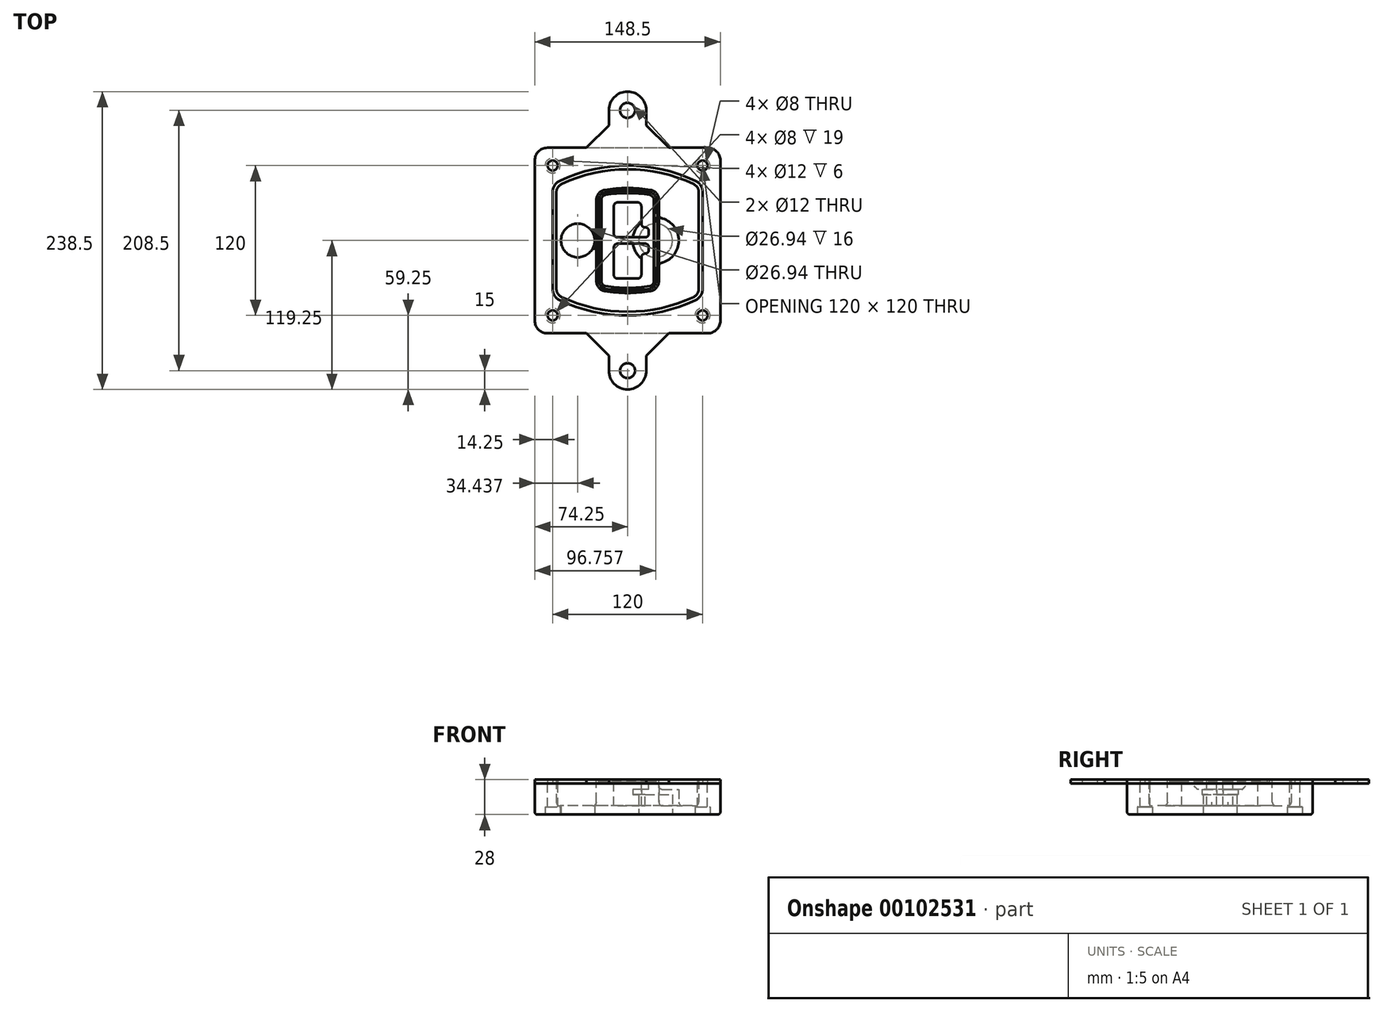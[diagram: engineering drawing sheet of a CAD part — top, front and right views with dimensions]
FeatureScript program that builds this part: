
annotation { "Feature Type Name" : "Feature", "Feature Type Description" : "" }
export const myFeature = defineFeature(function(context is Context, id is Id, definition is map)
    precondition{}
    {
        {
            var Q0;
            Q0=qCreatedBy(makeId("Top.planeOp"),FACE);
            var sketch = newSketch(context, id + "F0", { "sketchPlane" : qUnion([Q0])});
            skPoint(sketch, "E0.rect.middle", {"position": v(0, 0) * mm});
            skLineSegment(sketch, "E1.bottom", {"start": v(-64.25, -74.25) * mm, "end": v(64.25, -74.25) * mm});
            skLineSegment(sketch, "E1.top", {"start": v(-64.25, 74.25) * mm, "end": v(64.25, 74.25) * mm});
            skLineSegment(sketch, "E1.left", {"start": v(-74.25, -64.25) * mm, "end": v(-74.25, 64.25) * mm});
            skLineSegment(sketch, "E1.right", {"start": v(74.25, -64.25) * mm, "end": v(74.25, 64.25) * mm});
            skLineSegment(sketch, "E2", {"start": v(-74.25, 74.25) * mm, "end": v(74.25, -74.25) * mm, "construction": true});
            skLineSegment(sketch, "E3", {"start": v(74.25, 74.25) * mm, "end": v(-74.25, -74.25) * mm, "construction": true});
            skCircle(sketch, "E4", {"center": v(-60, 60) * mm, "radius": 4 * mm});
            skCircle(sketch, "E5", {"center": v(60, 60) * mm, "radius": 4 * mm});
            skCircle(sketch, "E6", {"center": v(60, -60) * mm, "radius": 4 * mm});
            skCircle(sketch, "E7", {"center": v(-60, -60) * mm, "radius": 4 * mm});
            skLineSegment(sketch, "E8", {"start": v(-60, 60) * mm, "end": v(60, 60) * mm, "construction": true});
            skLineSegment(sketch, "E9", {"start": v(60, 60) * mm, "end": v(60, -60) * mm, "construction": true});
            skLineSegment(sketch, "E10", {"start": v(60, -60) * mm, "end": v(-60, -60) * mm, "construction": true});
            skLineSegment(sketch, "E11", {"start": v(-60, -60) * mm, "end": v(-60, 60) * mm, "construction": true});
            skLineSegment(sketch, "E12", {"start": v(-60, 38.83) * mm, "end": v(-60, -38.83) * mm});
            skLineSegment(sketch, "E13", {"start": v(60, 38.83) * mm, "end": v(60, -38.83) * mm});
            skArc(sketch, "E14", {"start": v(54.26, 47.88) * mm, "mid": v(0, 60) * mm, "end": v(-54.26, 47.88) * mm});
            skArc(sketch, "E15", {"start": v(-54.26, -47.88) * mm, "mid": v(0, -60) * mm, "end": v(54.26, -47.88) * mm});
            skLineSegment(sketch, "E16", {"start": v(-60, 0) * mm, "end": v(60, 0) * mm, "construction": true});
            skPoint(sketch, "E17.visualSharp", {"position": v(-60, -45) * mm});
            skArc(sketch, "E17.filletArc", {"start": v(-60, -38.83) * mm, "mid": v(-58.44, -44.2) * mm, "end": v(-54.26, -47.88) * mm});
            skPoint(sketch, "E18.visualSharp", {"position": v(-60, 45) * mm});
            skArc(sketch, "E18.filletArc", {"start": v(-54.26, 47.88) * mm, "mid": v(-58.44, 44.2) * mm, "end": v(-60, 38.83) * mm});
            skPoint(sketch, "E19.visualSharp", {"position": v(60, 45) * mm});
            skArc(sketch, "E19.filletArc", {"start": v(60, 38.83) * mm, "mid": v(58.44, 44.2) * mm, "end": v(54.26, 47.88) * mm});
            skPoint(sketch, "E20.visualSharp", {"position": v(60, -45) * mm});
            skArc(sketch, "E20.filletArc", {"start": v(54.26, -47.88) * mm, "mid": v(58.44, -44.2) * mm, "end": v(60, -38.83) * mm});
            skPoint(sketch, "E21.visualSharp", {"position": v(-74.25, 74.25) * mm});
            skArc(sketch, "E21.filletArc", {"start": v(-64.25, 74.25) * mm, "mid": v(-71.32, 71.32) * mm, "end": v(-74.25, 64.25) * mm});
            skPoint(sketch, "E22.visualSharp", {"position": v(74.25, 74.25) * mm});
            skArc(sketch, "E22.filletArc", {"start": v(74.25, 64.25) * mm, "mid": v(71.32, 71.32) * mm, "end": v(64.25, 74.25) * mm});
            skPoint(sketch, "E23.visualSharp", {"position": v(74.25, -74.25) * mm});
            skArc(sketch, "E23.filletArc", {"start": v(64.25, -74.25) * mm, "mid": v(71.32, -71.32) * mm, "end": v(74.25, -64.25) * mm});
            skPoint(sketch, "E24.visualSharp", {"position": v(-74.25, -74.25) * mm});
            skArc(sketch, "E24.filletArc", {"start": v(-74.25, -64.25) * mm, "mid": v(-71.32, -71.32) * mm, "end": v(-64.25, -74.25) * mm});
            skArc(sketch, "E25.0", {"start": v(57, 38.83) * mm, "mid": v(55.9, 42.58) * mm, "end": v(52.98, 45.17) * mm});
            skLineSegment(sketch, "E25.1", {"start": v(57, 38.83) * mm, "end": v(57, -38.83) * mm});
            skArc(sketch, "E25.2", {"start": v(52.98, -45.17) * mm, "mid": v(55.9, -42.58) * mm, "end": v(57, -38.83) * mm});
            skArc(sketch, "E25.3", {"start": v(-52.98, -45.17) * mm, "mid": v(0, -57) * mm, "end": v(52.98, -45.17) * mm});
            skArc(sketch, "E25.4", {"start": v(-57, -38.83) * mm, "mid": v(-55.9, -42.58) * mm, "end": v(-52.98, -45.17) * mm});
            skArc(sketch, "E25.5", {"start": v(52.98, 45.17) * mm, "mid": v(0, 57) * mm, "end": v(-52.98, 45.17) * mm});
            skLineSegment(sketch, "E25.6", {"start": v(-57, 38.83) * mm, "end": v(-57, -38.83) * mm});
            skArc(sketch, "E25.7", {"start": v(-52.98, 45.17) * mm, "mid": v(-55.9, 42.58) * mm, "end": v(-57, 38.83) * mm});
            skArc(sketch, "E26.0", {"start": v(-55.96, 51.5) * mm, "mid": v(-61.82, 46.33) * mm, "end": v(-64, 38.83) * mm});
            skArc(sketch, "E26.1", {"start": v(55.96, 51.5) * mm, "mid": v(0, 64) * mm, "end": v(-55.96, 51.5) * mm});
            skArc(sketch, "E26.2", {"start": v(64, 38.83) * mm, "mid": v(61.82, 46.33) * mm, "end": v(55.96, 51.5) * mm});
            skLineSegment(sketch, "E26.3", {"start": v(64, 38.83) * mm, "end": v(64, -38.83) * mm});
            skArc(sketch, "E26.4", {"start": v(55.96, -51.5) * mm, "mid": v(61.82, -46.33) * mm, "end": v(64, -38.83) * mm});
            skLineSegment(sketch, "E26.5", {"start": v(-64, 38.83) * mm, "end": v(-64, -38.83) * mm});
            skArc(sketch, "E26.6", {"start": v(-55.96, -51.5) * mm, "mid": v(0, -64) * mm, "end": v(55.96, -51.5) * mm});
            skArc(sketch, "E26.7", {"start": v(-64, -38.83) * mm, "mid": v(-61.82, -46.33) * mm, "end": v(-55.96, -51.5) * mm});
            skSolve(sketch);
        }
        {
            var Q0;
            Q0=makeQuery(id+"F0.imprint","IMPRINT",FACE,{"disambiguationData":[TD([[makeQuery(id+"F0.imprint","IMPRINT",EDGE,{"derivedFrom":sQuery(id+"F0.wireOp",EDGE,"E1.bottom")}),1.0]])]});
            var Q1;
            Q1=makeQuery(id+"F0.imprint","IMPRINT",FACE,{"disambiguationData":[TD([[makeQuery(id+"F0.imprint","IMPRINT",EDGE,{"derivedFrom":sQuery(id+"F0.wireOp",EDGE,"E12")}),1.0]])]});
            var Q2;
            Q2=makeQuery(id+"F0.imprint","IMPRINT",FACE,{"disambiguationData":[TD([[makeQuery(id+"F0.imprint","IMPRINT",EDGE,{"derivedFrom":sQuery(id+"F0.wireOp",EDGE,"E25.0")}),1.0]])]});
            var Q3;
            Q3=makeQuery(id+"F0.imprint","IMPRINT",FACE,{"disambiguationData":[TD([[makeQuery(id+"F0.imprint","IMPRINT",EDGE,{"derivedFrom":sQuery(id+"F0.wireOp",EDGE,"E12")}),-1.0]])]});
            extrude(context, id + "F1", {"entities" : qUnion([Q0, Q1, Q2, Q3]), "oppositeDirection" : true, "depth" : 25 * mm});
        }
        {
            var Q0;
            Q0=makeQuery(id+"F0.imprint","IMPRINT",FACE,{"disambiguationData":[TD([[makeQuery(id+"F0.imprint","IMPRINT",EDGE,{"derivedFrom":sQuery(id+"F0.wireOp",EDGE,"E12")}),1.0]])]});
            extrude(context, id + "F2", {"entities" : qUnion([Q0]), "operationType" : NewBodyOperationType.ADD, "depth" : 3 * mm});
        }
        {
            var Q0;
            Q0=makeQuery(id+"F0.imprint","IMPRINT",FACE,{"disambiguationData":[TD([[makeQuery(id+"F0.imprint","IMPRINT",EDGE,{"derivedFrom":sQuery(id+"F0.wireOp",EDGE,"E25.0")}),1.0]])]});
            extrude(context, id + "F3", {"entities" : qUnion([Q0]), "operationType" : NewBodyOperationType.REMOVE, "oppositeDirection" : true, "depth" : 18 * mm});
        }
        {
            var Q0;
            Q0=makeQuery(id+"F2.opExtrude","CAP_FACE",FACE,{"disambiguationData":[OSD([sQuery(id+"F0.wireOp",EDGE,"E12"),sQuery(id+"F0.wireOp",EDGE,"E13"),sQuery(id+"F0.wireOp",EDGE,"E14"),sQuery(id+"F0.wireOp",EDGE,"E15"),sQuery(id+"F0.wireOp",EDGE,"E17.filletArc"),sQuery(id+"F0.wireOp",EDGE,"E18.filletArc"),sQuery(id+"F0.wireOp",EDGE,"E19.filletArc"),sQuery(id+"F0.wireOp",EDGE,"E20.filletArc"),sQuery(id+"F0.wireOp",EDGE,"E25.0"),sQuery(id+"F0.wireOp",EDGE,"E25.1"),sQuery(id+"F0.wireOp",EDGE,"E25.2"),sQuery(id+"F0.wireOp",EDGE,"E25.3"),sQuery(id+"F0.wireOp",EDGE,"E25.4"),sQuery(id+"F0.wireOp",EDGE,"E25.5"),sQuery(id+"F0.wireOp",EDGE,"E25.6"),sQuery(id+"F0.wireOp",EDGE,"E25.7")])],"isStart":false});
            var sketch = newSketch(context, id + "F4", { "sketchPlane" : qUnion([Q0])});
            skArc(sketch, "E27.0", {"start": v(-18.34, -40.45) * mm, "mid": v(0, -42) * mm, "end": v(18.34, -40.45) * mm});
            skArc(sketch, "E28.0", {"start": v(18.34, 40.45) * mm, "mid": v(0, 42) * mm, "end": v(-18.34, 40.45) * mm});
            skLineSegment(sketch, "E29", {"start": v(-25, 32.57) * mm, "end": v(-25, -32.57) * mm});
            skLineSegment(sketch, "E30", {"start": v(25, 32.57) * mm, "end": v(25, -32.57) * mm});
            skLineSegment(sketch, "E31", {"start": v(-25, 39.1) * mm, "end": v(25, 39.1) * mm, "construction": true});
            skLineSegment(sketch, "E32", {"start": v(-25, -39.1) * mm, "end": v(25, -39.1) * mm, "construction": true});
            skPoint(sketch, "E33.visualSharp", {"position": v(-25, 39.1) * mm});
            skArc(sketch, "E33.filletArc", {"start": v(-18.34, 40.45) * mm, "mid": v(-23.11, 37.73) * mm, "end": v(-25, 32.57) * mm});
            skPoint(sketch, "E34.visualSharp", {"position": v(25, 39.1) * mm});
            skArc(sketch, "E34.filletArc", {"start": v(25, 32.57) * mm, "mid": v(23.11, 37.73) * mm, "end": v(18.34, 40.45) * mm});
            skPoint(sketch, "E35.visualSharp", {"position": v(25, -39.1) * mm});
            skArc(sketch, "E35.filletArc", {"start": v(18.34, -40.45) * mm, "mid": v(23.11, -37.73) * mm, "end": v(25, -32.57) * mm});
            skPoint(sketch, "E36.visualSharp", {"position": v(-25, -39.1) * mm});
            skArc(sketch, "E36.filletArc", {"start": v(-25, -32.57) * mm, "mid": v(-23.11, -37.73) * mm, "end": v(-18.34, -40.45) * mm});
            skArc(sketch, "E37.0", {"start": v(52.98, 45.17) * mm, "mid": v(0, 57) * mm, "end": v(-52.98, 45.17) * mm});
            skArc(sketch, "E37.1", {"start": v(-52.98, 45.17) * mm, "mid": v(-55.9, 42.58) * mm, "end": v(-57, 38.83) * mm});
            skLineSegment(sketch, "E37.2", {"start": v(-57, 38.83) * mm, "end": v(-57, -38.83) * mm});
            skArc(sketch, "E37.3", {"start": v(-57, -38.83) * mm, "mid": v(-55.9, -42.58) * mm, "end": v(-52.98, -45.17) * mm});
            skArc(sketch, "E37.4", {"start": v(-52.98, -45.17) * mm, "mid": v(0, -57) * mm, "end": v(52.98, -45.17) * mm});
            skArc(sketch, "E37.5", {"start": v(52.98, -45.17) * mm, "mid": v(55.9, -42.58) * mm, "end": v(57, -38.83) * mm});
            skLineSegment(sketch, "E37.6", {"start": v(57, 38.83) * mm, "end": v(57, -38.83) * mm});
            skArc(sketch, "E37.7", {"start": v(57, 38.83) * mm, "mid": v(55.9, 42.58) * mm, "end": v(52.98, 45.17) * mm});
            skLineSegment(sketch, "E38.0", {"start": v(23, 32.57) * mm, "end": v(23, -32.57) * mm});
            skArc(sketch, "E38.1", {"start": v(18, -38.48) * mm, "mid": v(21.58, -36.44) * mm, "end": v(23, -32.57) * mm});
            skArc(sketch, "E38.2", {"start": v(-18, -38.48) * mm, "mid": v(0, -40) * mm, "end": v(18, -38.48) * mm});
            skArc(sketch, "E38.3", {"start": v(-23, -32.57) * mm, "mid": v(-21.58, -36.44) * mm, "end": v(-18, -38.48) * mm});
            skLineSegment(sketch, "E38.4", {"start": v(-23, 32.57) * mm, "end": v(-23, -32.57) * mm});
            skArc(sketch, "E38.5", {"start": v(23, 32.57) * mm, "mid": v(21.58, 36.44) * mm, "end": v(18, 38.48) * mm});
            skArc(sketch, "E38.6", {"start": v(-18, 38.48) * mm, "mid": v(-21.58, 36.44) * mm, "end": v(-23, 32.57) * mm});
            skArc(sketch, "E38.7", {"start": v(18, 38.48) * mm, "mid": v(0, 40) * mm, "end": v(-18, 38.48) * mm});
            skArc(sketch, "E39.0", {"start": v(21, 32.57) * mm, "mid": v(20.06, 35.15) * mm, "end": v(17.67, 36.5) * mm});
            skLineSegment(sketch, "E39.1", {"start": v(21, 32.57) * mm, "end": v(21, -32.57) * mm});
            skArc(sketch, "E39.2", {"start": v(17.67, -36.5) * mm, "mid": v(20.06, -35.15) * mm, "end": v(21, -32.57) * mm});
            skArc(sketch, "E39.3", {"start": v(-17.67, -36.5) * mm, "mid": v(0, -38) * mm, "end": v(17.67, -36.5) * mm});
            skArc(sketch, "E39.4", {"start": v(-21, -32.57) * mm, "mid": v(-20.06, -35.15) * mm, "end": v(-17.67, -36.5) * mm});
            skArc(sketch, "E39.5", {"start": v(17.67, 36.5) * mm, "mid": v(0, 38) * mm, "end": v(-17.67, 36.5) * mm});
            skLineSegment(sketch, "E39.6", {"start": v(-21, 32.57) * mm, "end": v(-21, -32.57) * mm});
            skArc(sketch, "E39.7", {"start": v(-17.67, 36.5) * mm, "mid": v(-20.06, 35.15) * mm, "end": v(-21, 32.57) * mm});
            skLineSegment(sketch, "E40", {"start": v(-25, 0) * mm, "end": v(25, 0) * mm, "construction": true});
            skLineSegment(sketch, "E41", {"start": v(-11, 5.5) * mm, "end": v(-11, 27.5) * mm});
            skLineSegment(sketch, "E42", {"start": v(-8, 30.5) * mm, "end": v(8, 30.5) * mm});
            skLineSegment(sketch, "E43", {"start": v(11, 27.5) * mm, "end": v(11, 13.5) * mm});
            skLineSegment(sketch, "E44", {"start": v(14, 10.5) * mm, "end": v(14, 10.5) * mm});
            skLineSegment(sketch, "E45", {"start": v(17, 7.5) * mm, "end": v(17, 5.5) * mm});
            skLineSegment(sketch, "E46", {"start": v(14, 2.5) * mm, "end": v(-8, 2.5) * mm});
            skPoint(sketch, "E47.visualSharp", {"position": v(-11, 30.5) * mm});
            skArc(sketch, "E47.filletArc", {"start": v(-8, 30.5) * mm, "mid": v(-10.12, 29.62) * mm, "end": v(-11, 27.5) * mm});
            skPoint(sketch, "E48.visualSharp", {"position": v(11, 30.5) * mm});
            skArc(sketch, "E48.filletArc", {"start": v(11, 27.5) * mm, "mid": v(10.12, 29.62) * mm, "end": v(8, 30.5) * mm});
            skPoint(sketch, "E49.visualSharp", {"position": v(11, 10.5) * mm});
            skArc(sketch, "E49.filletArc", {"start": v(11, 13.5) * mm, "mid": v(11.88, 11.38) * mm, "end": v(14, 10.5) * mm});
            skPoint(sketch, "E50.visualSharp", {"position": v(17, 10.5) * mm});
            skArc(sketch, "E50.filletArc", {"start": v(17, 7.5) * mm, "mid": v(16.12, 9.62) * mm, "end": v(14, 10.5) * mm});
            skPoint(sketch, "E51.visualSharp", {"position": v(17, 2.5) * mm});
            skArc(sketch, "E51.filletArc", {"start": v(14, 2.5) * mm, "mid": v(16.12, 3.38) * mm, "end": v(17, 5.5) * mm});
            skPoint(sketch, "E52.visualSharp", {"position": v(-11, 2.5) * mm});
            skArc(sketch, "E52.filletArc", {"start": v(-11, 5.5) * mm, "mid": v(-10.12, 3.38) * mm, "end": v(-8, 2.5) * mm});
            skLineSegment(sketch, "E53.0.MirrorCS", {"start": v(14, -2.5) * mm, "end": v(-8, -2.5) * mm});
            skArc(sketch, "E54.0.MirrorCS", {"start": v(-11, -5.5) * mm, "mid": v(-10.12, -3.38) * mm, "end": v(-8, -2.5) * mm});
            skLineSegment(sketch, "E55.0.MirrorCS", {"start": v(-11, -5.5) * mm, "end": v(-11, -27.5) * mm});
            skArc(sketch, "E56.0.MirrorCS", {"start": v(-8, -30.5) * mm, "mid": v(-10.12, -29.62) * mm, "end": v(-11, -27.5) * mm});
            skLineSegment(sketch, "E57.0.MirrorCS", {"start": v(-8, -30.5) * mm, "end": v(8, -30.5) * mm});
            skArc(sketch, "E58.0.MirrorCS", {"start": v(11, -27.5) * mm, "mid": v(10.12, -29.62) * mm, "end": v(8, -30.5) * mm});
            skLineSegment(sketch, "E59.0.MirrorCS", {"start": v(11, -27.5) * mm, "end": v(11, -13.5) * mm});
            skArc(sketch, "E60.0.MirrorCS", {"start": v(11, -13.5) * mm, "mid": v(11.88, -11.38) * mm, "end": v(14, -10.5) * mm});
            skArc(sketch, "E61.0.MirrorCS", {"start": v(17, -7.5) * mm, "mid": v(16.12, -9.62) * mm, "end": v(14, -10.5) * mm});
            skLineSegment(sketch, "E62.0.MirrorCS", {"start": v(17, -7.5) * mm, "end": v(17, -5.5) * mm});
            skArc(sketch, "E63.0.MirrorCS", {"start": v(14, -2.5) * mm, "mid": v(16.12, -3.38) * mm, "end": v(17, -5.5) * mm});
            skSolve(sketch);
        }
        {
            var Q0;
            Q0=makeQuery(id+"F4.imprint","IMPRINT",FACE,{"disambiguationData":[TD([[makeQuery(id+"F4.imprint","IMPRINT",EDGE,{"derivedFrom":sQuery(id+"F4.wireOp",EDGE,"E27.0")}),1.0]])]});
            var Q1;
            Q1=makeQuery(id+"F4.imprint","IMPRINT",FACE,{"disambiguationData":[TD([[makeQuery(id+"F4.imprint","IMPRINT",EDGE,{"derivedFrom":sQuery(id+"F4.wireOp",EDGE,"E38.0")}),-1.0]])]});
            var Q2;
            Q2=makeQuery(id+"F4.imprint","IMPRINT",FACE,{"disambiguationData":[TD([[makeQuery(id+"F4.imprint","IMPRINT",EDGE,{"derivedFrom":sQuery(id+"F4.wireOp",EDGE,"E39.0")}),1.0]])]});
            extrude(context, id + "F5", {"entities" : qUnion([Q0, Q1, Q2]), "operationType" : NewBodyOperationType.ADD, "endBound" : BoundingType.UP_TO_NEXT, "oppositeDirection" : true, "depth" : 25 * mm});
        }
        {
            var Q0;
            Q0=makeQuery(id+"F4.imprint","IMPRINT",FACE,{"disambiguationData":[TD([[makeQuery(id+"F4.imprint","IMPRINT",EDGE,{"derivedFrom":sQuery(id+"F4.wireOp",EDGE,"E38.0")}),-1.0]])]});
            extrude(context, id + "F6", {"entities" : qUnion([Q0]), "operationType" : NewBodyOperationType.REMOVE, "oppositeDirection" : true, "depth" : 2 * mm});
        }
        {
            var Q0;
            Q0=makeQuery(id+"F1.opExtrude","CAP_FACE",FACE,{"disambiguationData":[OSD([sQuery(id+"F0.wireOp",EDGE,"E1.bottom"),sQuery(id+"F0.wireOp",EDGE,"E1.top"),sQuery(id+"F0.wireOp",EDGE,"E1.left"),sQuery(id+"F0.wireOp",EDGE,"E1.right"),sQuery(id+"F0.wireOp",EDGE,"E4"),sQuery(id+"F0.wireOp",EDGE,"E5"),sQuery(id+"F0.wireOp",EDGE,"E6"),sQuery(id+"F0.wireOp",EDGE,"E7"),sQuery(id+"F0.wireOp",EDGE,"E21.filletArc"),sQuery(id+"F0.wireOp",EDGE,"E22.filletArc"),sQuery(id+"F0.wireOp",EDGE,"E23.filletArc"),sQuery(id+"F0.wireOp",EDGE,"E24.filletArc")])],"isStart":false});
            var sketch = newSketch(context, id + "F7", { "sketchPlane" : qUnion([Q0])});
            skCircle(sketch, "E64", {"center": v(22.5, 0) * mm, "radius": 13.47 * mm});
            skCircle(sketch, "E65", {"center": v(-39.81, 0) * mm, "radius": 13.47 * mm});
            skLineSegment(sketch, "E66", {"start": v(74.25, 0) * mm, "end": v(-74.25, 0) * mm});
            skCircle(sketch, "E67", {"center": v(22.5, 0) * mm, "radius": 18.47 * mm});
            skCircle(sketch, "E68", {"center": v(60, -60) * mm, "radius": 6 * mm});
            skCircle(sketch, "E69", {"center": v(-60, -60) * mm, "radius": 6 * mm});
            skCircle(sketch, "E70", {"center": v(-60, 60) * mm, "radius": 6 * mm});
            skCircle(sketch, "E71", {"center": v(60, 60) * mm, "radius": 6 * mm});
            skSolve(sketch);
        }
        {
            var Q0;
            {var subQ1=sQuery(id+"F7.wireOp",EDGE,"E66");var subQ4=sQuery(id+"F7.wireOp",EDGE,"E64");var subQ6=makeQuery(id+"F7.imprint","INTERSECT",VERTEX,{"disambiguationData":[OD(0.0)],"derivedFrom":[subQ4,subQ1]});Q0=makeQuery(id+"F7.imprint","IMPRINT",FACE,{"disambiguationData":[TD([[makeQuery(id+"F7.imprint","IMPRINT",EDGE,{"disambiguationData":[TD([[subQ6,-1.0]])],"derivedFrom":subQ4}),-1.0]])]});}
            var Q1;
            {var subQ0=sQuery(id+"F7.wireOp",EDGE,"E66");var subQ1=sQuery(id+"F7.wireOp",EDGE,"E64");var subQ3=makeQuery(id+"F7.imprint","INTERSECT",VERTEX,{"disambiguationData":[OD(0.0)],"derivedFrom":[subQ1,subQ0]});Q1=makeQuery(id+"F7.imprint","IMPRINT",FACE,{"disambiguationData":[TD([[makeQuery(id+"F7.imprint","IMPRINT",EDGE,{"disambiguationData":[TD([[subQ3,-1.0]])],"derivedFrom":subQ1}),1.0]])]});}
            var Q2;
            {var subQ0=sQuery(id+"F7.wireOp",EDGE,"E66");var subQ1=sQuery(id+"F7.wireOp",EDGE,"E64");var subQ3=makeQuery(id+"F7.imprint","INTERSECT",VERTEX,{"disambiguationData":[OD(0.0)],"derivedFrom":[subQ1,subQ0]});Q2=makeQuery(id+"F7.imprint","IMPRINT",FACE,{"disambiguationData":[TD([[makeQuery(id+"F7.imprint","IMPRINT",EDGE,{"disambiguationData":[TD([[subQ3,1.0]])],"derivedFrom":subQ1}),1.0]])]});}
            var Q3;
            {var subQ1=sQuery(id+"F7.wireOp",EDGE,"E66");var subQ4=sQuery(id+"F7.wireOp",EDGE,"E64");var subQ6=makeQuery(id+"F7.imprint","INTERSECT",VERTEX,{"disambiguationData":[OD(0.0)],"derivedFrom":[subQ4,subQ1]});Q3=makeQuery(id+"F7.imprint","IMPRINT",FACE,{"disambiguationData":[TD([[makeQuery(id+"F7.imprint","IMPRINT",EDGE,{"disambiguationData":[TD([[subQ6,1.0]])],"derivedFrom":subQ4}),-1.0]])]});}
            extrude(context, id + "F8", {"entities" : qUnion([Q0, Q1, Q2, Q3]), "operationType" : NewBodyOperationType.ADD, "oppositeDirection" : true, "depth" : 20 * mm});
        }
        {
            var Q0;
            {var subQ0=sQuery(id+"F7.wireOp",EDGE,"E66");var subQ1=sQuery(id+"F7.wireOp",EDGE,"E64");var subQ3=makeQuery(id+"F7.imprint","INTERSECT",VERTEX,{"disambiguationData":[OD(0.0)],"derivedFrom":[subQ1,subQ0]});Q0=makeQuery(id+"F7.imprint","IMPRINT",FACE,{"disambiguationData":[TD([[makeQuery(id+"F7.imprint","IMPRINT",EDGE,{"disambiguationData":[TD([[subQ3,-1.0]])],"derivedFrom":subQ1}),1.0]])]});}
            var Q1;
            {var subQ0=sQuery(id+"F7.wireOp",EDGE,"E66");var subQ1=sQuery(id+"F7.wireOp",EDGE,"E64");var subQ3=makeQuery(id+"F7.imprint","INTERSECT",VERTEX,{"disambiguationData":[OD(0.0)],"derivedFrom":[subQ1,subQ0]});Q1=makeQuery(id+"F7.imprint","IMPRINT",FACE,{"disambiguationData":[TD([[makeQuery(id+"F7.imprint","IMPRINT",EDGE,{"disambiguationData":[TD([[subQ3,1.0]])],"derivedFrom":subQ1}),1.0]])]});}
            extrude(context, id + "F9", {"entities" : qUnion([Q0, Q1]), "operationType" : NewBodyOperationType.REMOVE, "oppositeDirection" : true, "depth" : 16 * mm});
        }
        {
            var Q0;
            {var subQ0=sQuery(id+"F7.wireOp",EDGE,"E66");var subQ1=sQuery(id+"F7.wireOp",EDGE,"E65");var subQ3=makeQuery(id+"F7.imprint","INTERSECT",VERTEX,{"disambiguationData":[OD(0.0)],"derivedFrom":[subQ1,subQ0]});Q0=makeQuery(id+"F7.imprint","IMPRINT",FACE,{"disambiguationData":[TD([[makeQuery(id+"F7.imprint","IMPRINT",EDGE,{"disambiguationData":[TD([[subQ3,-1.0]])],"derivedFrom":subQ1}),1.0]])]});}
            var Q1;
            {var subQ0=sQuery(id+"F7.wireOp",EDGE,"E66");var subQ1=sQuery(id+"F7.wireOp",EDGE,"E65");var subQ3=makeQuery(id+"F7.imprint","INTERSECT",VERTEX,{"disambiguationData":[OD(0.0)],"derivedFrom":[subQ1,subQ0]});Q1=makeQuery(id+"F7.imprint","IMPRINT",FACE,{"disambiguationData":[TD([[makeQuery(id+"F7.imprint","IMPRINT",EDGE,{"disambiguationData":[TD([[subQ3,1.0]])],"derivedFrom":subQ1}),1.0]])]});}
            extrude(context, id + "F10", {"entities" : qUnion([Q0, Q1]), "operationType" : NewBodyOperationType.REMOVE, "oppositeDirection" : true, "depth" : 25 * mm});
        }
        {
            var Q0;
            Q0=makeQuery(id+"F7.imprint","IMPRINT",FACE,{"disambiguationData":[TD([[makeQuery(id+"F7.imprint","IMPRINT",EDGE,{"derivedFrom":sQuery(id+"F7.wireOp",EDGE,"E68")}),1.0]])]});
            var Q1;
            Q1=makeQuery(id+"F7.imprint","IMPRINT",FACE,{"disambiguationData":[TD([[makeQuery(id+"F7.imprint","IMPRINT",EDGE,{"derivedFrom":makeQuery(id+"F1.opExtrude","CAP_EDGE",EDGE,{"disambiguationData":[OSD([sQuery(id+"F0.wireOp",EDGE,"E5")])],"isStart":false})}),-1.0]])]});
            var Q2;
            Q2=makeQuery(id+"F7.imprint","IMPRINT",FACE,{"disambiguationData":[TD([[makeQuery(id+"F7.imprint","IMPRINT",EDGE,{"derivedFrom":sQuery(id+"F7.wireOp",EDGE,"E69")}),1.0]])]});
            var Q3;
            Q3=makeQuery(id+"F7.imprint","IMPRINT",FACE,{"disambiguationData":[TD([[makeQuery(id+"F7.imprint","IMPRINT",EDGE,{"derivedFrom":makeQuery(id+"F1.opExtrude","CAP_EDGE",EDGE,{"disambiguationData":[OSD([sQuery(id+"F0.wireOp",EDGE,"E4")])],"isStart":false})}),-1.0]])]});
            var Q4;
            Q4=makeQuery(id+"F7.imprint","IMPRINT",FACE,{"disambiguationData":[TD([[makeQuery(id+"F7.imprint","IMPRINT",EDGE,{"derivedFrom":sQuery(id+"F7.wireOp",EDGE,"E70")}),1.0]])]});
            var Q5;
            Q5=makeQuery(id+"F7.imprint","IMPRINT",FACE,{"disambiguationData":[TD([[makeQuery(id+"F7.imprint","IMPRINT",EDGE,{"derivedFrom":makeQuery(id+"F1.opExtrude","CAP_EDGE",EDGE,{"disambiguationData":[OSD([sQuery(id+"F0.wireOp",EDGE,"E7")])],"isStart":false})}),-1.0]])]});
            var Q6;
            Q6=makeQuery(id+"F7.imprint","IMPRINT",FACE,{"disambiguationData":[TD([[makeQuery(id+"F7.imprint","IMPRINT",EDGE,{"derivedFrom":sQuery(id+"F7.wireOp",EDGE,"E71")}),1.0]])]});
            var Q7;
            Q7=makeQuery(id+"F7.imprint","IMPRINT",FACE,{"disambiguationData":[TD([[makeQuery(id+"F7.imprint","IMPRINT",EDGE,{"derivedFrom":makeQuery(id+"F1.opExtrude","CAP_EDGE",EDGE,{"disambiguationData":[OSD([sQuery(id+"F0.wireOp",EDGE,"E6")])],"isStart":false})}),-1.0]])]});
            extrude(context, id + "F11", {"entities" : qUnion([Q0, Q1, Q2, Q3, Q4, Q5, Q6, Q7]), "operationType" : NewBodyOperationType.REMOVE, "oppositeDirection" : true, "depth" : 6 * mm});
        }
        {
            var Q0;
            Q0=makeQuery(id+"F9.boolean.opBoolean","COPY",FACE,{"derivedFrom":makeQuery(id+"F9.opExtrude","CAP_FACE",FACE,{"disambiguationData":[OSD([sQuery(id+"F7.wireOp",EDGE,"E64")])],"isStart":false})});
            var sketch = newSketch(context, id + "F12", { "sketchPlane" : qUnion([Q0])});
            skArc(sketch, "E72.0", {"start": v(11, 14.45) * mm, "mid": v(6.45, 9.13) * mm, "end": v(4.2, 2.5) * mm});
            skArc(sketch, "E72.1", {"start": v(4.2, -2.5) * mm, "mid": v(6.45, -9.13) * mm, "end": v(11, -14.45) * mm});
            skLineSegment(sketch, "E73", {"start": v(4.2, -2.5) * mm, "end": v(14, -2.5) * mm});
            skLineSegment(sketch, "E74.0", {"start": v(14, 2.5) * mm, "end": v(4.2, 2.5) * mm});
            skArc(sketch, "E74.1", {"start": v(14, 2.5) * mm, "mid": v(16.12, 3.38) * mm, "end": v(17, 5.5) * mm});
            skLineSegment(sketch, "E74.2", {"start": v(17, 7.5) * mm, "end": v(17, 5.5) * mm});
            skArc(sketch, "E74.3", {"start": v(17, 7.5) * mm, "mid": v(16.12, 9.62) * mm, "end": v(14, 10.5) * mm});
            skArc(sketch, "E74.4", {"start": v(11, 13.5) * mm, "mid": v(11.88, 11.38) * mm, "end": v(14, 10.5) * mm});
            skLineSegment(sketch, "E74.5", {"start": v(11, 14.45) * mm, "end": v(11, 13.5) * mm});
            skLineSegment(sketch, "E74.7", {"start": v(14, -2.5) * mm, "end": v(4.2, -2.5) * mm});
            skArc(sketch, "E74.8", {"start": v(14, -2.5) * mm, "mid": v(16.12, -3.38) * mm, "end": v(17, -5.5) * mm});
            skLineSegment(sketch, "E74.9", {"start": v(17, -7.5) * mm, "end": v(17, -5.5) * mm});
            skArc(sketch, "E74.10", {"start": v(17, -7.5) * mm, "mid": v(16.12, -9.62) * mm, "end": v(14, -10.5) * mm});
            skArc(sketch, "E74.11", {"start": v(11, -13.5) * mm, "mid": v(11.88, -11.38) * mm, "end": v(14, -10.5) * mm});
            skLineSegment(sketch, "E74.12", {"start": v(11, -14.45) * mm, "end": v(11, -13.5) * mm});
            skPoint(sketch, "E75.orphan", {"position": v(11, -27.5) * mm});
            skPoint(sketch, "E76.orphan", {"position": v(-8, -2.5) * mm});
            skPoint(sketch, "E77.orphan", {"position": v(-8, 2.5) * mm});
            skPoint(sketch, "E78.orphan", {"position": v(11, 27.5) * mm});
            skSolve(sketch);
        }
        {
            var Q0;
            {var subQ7=sQuery(id+"F12.wireOp",EDGE,"E72.0");var subQ14=sQuery(id+"F12.wireOp",EDGE,"E72.1");var subQ16=sQuery(id+"F12.wireOp",EDGE,"E74.1");var subQ18=sQuery(id+"F12.wireOp",EDGE,"E74.8");Q0=qUnion([makeQuery(id+"F12.imprint","IMPRINT",FACE,{"disambiguationData":[TD([[makeQuery(id+"F12.imprint","IMPRINT",EDGE,{"derivedFrom":subQ7}),1.0]])]}),makeQuery(id+"F12.imprint","IMPRINT",FACE,{"disambiguationData":[TD([[makeQuery(id+"F12.imprint","IMPRINT",EDGE,{"derivedFrom":subQ14}),1.0]])]}),makeQuery(id+"F12.imprint","IMPRINT",FACE,{"disambiguationData":[TD([[makeQuery(id+"F12.imprint","IMPRINT",EDGE,{"derivedFrom":subQ16}),1.0]])]}),makeQuery(id+"F12.imprint","IMPRINT",FACE,{"disambiguationData":[TD([[makeQuery(id+"F12.imprint","IMPRINT",EDGE,{"derivedFrom":subQ18}),-1.0]])]})]);}
            var Q1;
            Q1=makeQuery(id+"F5.boolean.opBoolean","SPLIT",FACE,{"disambiguationData":[TD([makeQuery(id+"F5.opExtrude","SWEPT_FACE",FACE,{"disambiguationData":[OSD([sQuery(id+"F4.wireOp",EDGE,"E41")])]})])],"derivedFrom":makeQuery(id+"F3.boolean.opBoolean","COPY",FACE,{"derivedFrom":makeQuery(id+"F3.opExtrude","CAP_FACE",FACE,{"disambiguationData":[OSD([sQuery(id+"F0.wireOp",EDGE,"E25.0"),sQuery(id+"F0.wireOp",EDGE,"E25.1"),sQuery(id+"F0.wireOp",EDGE,"E25.2"),sQuery(id+"F0.wireOp",EDGE,"E25.3"),sQuery(id+"F0.wireOp",EDGE,"E25.4"),sQuery(id+"F0.wireOp",EDGE,"E25.5"),sQuery(id+"F0.wireOp",EDGE,"E25.6"),sQuery(id+"F0.wireOp",EDGE,"E25.7")])],"isStart":false})})});
            extrude(context, id + "F13", {"entities" : qUnion([Q0]), "operationType" : NewBodyOperationType.REMOVE, "endBound" : BoundingType.UP_TO_SURFACE, "endBoundEntityFace" : qUnion([Q1]), "depth" : 25 * mm});
        }
        {
            var Q0;
            Q0=makeQuery(id+"F3.boolean.opBoolean","COPY",EDGE,{"derivedFrom":makeQuery(id+"F3.opExtrude","CAP_EDGE",EDGE,{"disambiguationData":[OSD([sQuery(id+"F0.wireOp",EDGE,"E25.6")])],"isStart":false})});
            var Q1;
            Q1=makeQuery(id+"F8.boolean.opBoolean","INTERSECT",EDGE,{"derivedFrom":[makeQuery(id+"F5.opExtrude","SWEPT_FACE",FACE,{"disambiguationData":[OSD([sQuery(id+"F4.wireOp",EDGE,"E30")])]}),makeQuery(id+"F8.opExtrude","CAP_FACE",FACE,{"disambiguationData":[OSD([sQuery(id+"F7.wireOp",EDGE,"E67")])],"isStart":false})]});
            var Q2;
            Q2=makeQuery(id+"F8.boolean.opBoolean","INTERSECT",EDGE,{"disambiguationData":[OD(1.0)],"derivedFrom":[makeQuery(id+"F5.opExtrude","SWEPT_FACE",FACE,{"disambiguationData":[OSD([sQuery(id+"F4.wireOp",EDGE,"E30")])]}),makeQuery(id+"F8.opExtrude","SWEPT_FACE",FACE,{"disambiguationData":[OSD([sQuery(id+"F7.wireOp",EDGE,"E67")])]})]});
            var Q3;
            {var subQ0=sQuery(id+"F4.wireOp",EDGE,"E30");Q3=makeQuery(id+"F8.boolean.opBoolean","SPLIT",EDGE,{"disambiguationData":[TD([makeQuery(id+"F5.opExtrude","SWEPT_FACE",FACE,{"disambiguationData":[OSD([sQuery(id+"F4.wireOp",EDGE,"E35.filletArc")])]})])],"derivedFrom":makeQuery(id+"F5.opExtrude","CAP_EDGE",EDGE,{"disambiguationData":[OSD([subQ0])],"isStart":false})});}
            var Q4;
            {var subQ0=sQuery(id+"F0.wireOp",EDGE,"E25.7");var subQ1=sQuery(id+"F0.wireOp",EDGE,"E25.1");var subQ2=sQuery(id+"F0.wireOp",EDGE,"E25.6");var subQ3=sQuery(id+"F0.wireOp",EDGE,"E25.5");var subQ4=sQuery(id+"F0.wireOp",EDGE,"E25.4");var subQ5=sQuery(id+"F0.wireOp",EDGE,"E25.0");var subQ6=sQuery(id+"F0.wireOp",EDGE,"E25.2");var subQ7=sQuery(id+"F0.wireOp",EDGE,"E25.3");Q4=makeQuery(id+"F8.boolean.opBoolean","INTERSECT",EDGE,{"derivedFrom":[makeQuery(id+"F5.boolean.opBoolean","SPLIT",FACE,{"disambiguationData":[TD([makeQuery(id+"F2.opExtrude","SWEPT_FACE",FACE,{"disambiguationData":[OSD([subQ5])]})])],"derivedFrom":makeQuery(id+"F3.boolean.opBoolean","COPY",FACE,{"derivedFrom":makeQuery(id+"F3.opExtrude","CAP_FACE",FACE,{"disambiguationData":[OSD([subQ5,subQ1,subQ6,subQ7,subQ4,subQ3,subQ2,subQ0])],"isStart":false})})}),makeQuery(id+"F8.opExtrude","SWEPT_FACE",FACE,{"disambiguationData":[OSD([sQuery(id+"F7.wireOp",EDGE,"E67")])]})]});}
            var Q5;
            Q5=makeQuery(id+"F8.boolean.opBoolean","INTERSECT",EDGE,{"disambiguationData":[OD(0.0)],"derivedFrom":[makeQuery(id+"F5.opExtrude","SWEPT_FACE",FACE,{"disambiguationData":[OSD([sQuery(id+"F4.wireOp",EDGE,"E30")])]}),makeQuery(id+"F8.opExtrude","SWEPT_FACE",FACE,{"disambiguationData":[OSD([sQuery(id+"F7.wireOp",EDGE,"E67")])]})]});
            fillet(context, id + "F14", {"entities" : qUnion([Q0, Q1, Q2, Q3, Q4, Q5]), "radius" : 3 * mm, "tangentPropagation" : true, "allowEdgeOverflow" : false});
        }
        {
            var Q0;
            Q0=makeQuery(id+"F1.opExtrude","CAP_EDGE",EDGE,{"disambiguationData":[OSD([sQuery(id+"F0.wireOp",EDGE,"E1.bottom")])],"isStart":false});
            fillet(context, id + "F15", {"entities" : qUnion([Q0]), "radius" : 2 * mm, "tangentPropagation" : true, "allowEdgeOverflow" : false});
        }
        {
            var Q0;
            {var subQ0=sQuery(id+"F0.wireOp",EDGE,"E22.filletArc");var subQ1=sQuery(id+"F0.wireOp",EDGE,"E7");var subQ2=sQuery(id+"F0.wireOp",EDGE,"E6");var subQ3=sQuery(id+"F0.wireOp",EDGE,"E5");var subQ4=sQuery(id+"F0.wireOp",EDGE,"E4");var subQ5=sQuery(id+"F0.wireOp",EDGE,"E1.bottom");var subQ6=sQuery(id+"F0.wireOp",EDGE,"E21.filletArc");var subQ7=sQuery(id+"F0.wireOp",EDGE,"E1.top");var subQ8=sQuery(id+"F0.wireOp",EDGE,"E1.left");var subQ9=sQuery(id+"F0.wireOp",EDGE,"E1.right");var subQ10=sQuery(id+"F0.wireOp",EDGE,"E23.filletArc");var subQ11=sQuery(id+"F0.wireOp",EDGE,"E24.filletArc");Q0=makeQuery(id+"F2.boolean.opBoolean","SPLIT",FACE,{"disambiguationData":[TD([makeQuery(id+"F1.opExtrude","SWEPT_FACE",FACE,{"disambiguationData":[OSD([subQ5])]})])],"derivedFrom":makeQuery(id+"F1.opExtrude","CAP_FACE",FACE,{"disambiguationData":[OSD([subQ5,subQ7,subQ8,subQ9,subQ4,subQ3,subQ2,subQ1,subQ6,subQ0,subQ10,subQ11])],"isStart":true})});}
            var sketch = newSketch(context, id + "F16", { "sketchPlane" : qUnion([Q0])});
            skLineSegment(sketch, "E79", {"start": v(0, 74.25) * mm, "end": v(0, 104.25) * mm, "construction": true});
            skPoint(sketch, "E79.endSnap0", {"position": v(0, 74.25) * mm});
            skCircle(sketch, "E80", {"center": v(0, 104.25) * mm, "radius": 6 * mm});
            skLineSegment(sketch, "E81", {"start": v(-28.01, 74.25) * mm, "end": v(31.37, 74.25) * mm});
            skPoint(sketch, "E82.endSnap0", {"position": v(0, 89.25) * mm});
            skArc(sketch, "E83", {"start": v(15, 104.25) * mm, "mid": v(0, 119.25) * mm, "end": v(-15, 104.25) * mm});
            skLineSegment(sketch, "E84", {"start": v(-33, 74.25) * mm, "end": v(-15, 92.25) * mm});
            skLineSegment(sketch, "E85", {"start": v(-15, 92.25) * mm, "end": v(-15, 104.25) * mm});
            skLineSegment(sketch, "E86", {"start": v(15, 104.25) * mm, "end": v(15, 92.25) * mm});
            skLineSegment(sketch, "E87", {"start": v(15, 92.25) * mm, "end": v(33, 74.25) * mm});
            skLineSegment(sketch, "E88", {"start": v(-74.25, 0) * mm, "end": v(74.25, 0) * mm, "construction": true});
            skLineSegment(sketch, "E89.MirrorCS", {"start": v(-33, -74.25) * mm, "end": v(-15, -92.25) * mm});
            skLineSegment(sketch, "E90.MirrorCS", {"start": v(-28.01, -74.25) * mm, "end": v(31.37, -74.25) * mm});
            skLineSegment(sketch, "E91.MirrorCS", {"start": v(15, -92.25) * mm, "end": v(33, -74.25) * mm});
            skLineSegment(sketch, "E92.MirrorCS", {"start": v(15, -104.25) * mm, "end": v(15, -92.25) * mm});
            skArc(sketch, "E93.MirrorCS", {"start": v(15, -104.25) * mm, "mid": v(0, -119.25) * mm, "end": v(-15, -104.25) * mm});
            skLineSegment(sketch, "E94.MirrorCS", {"start": v(-15, -92.25) * mm, "end": v(-15, -104.25) * mm});
            skLineSegment(sketch, "E95.MirrorCS", {"start": v(0, -74.25) * mm, "end": v(0, -104.25) * mm, "construction": true});
            skCircle(sketch, "E96.MirrorC", {"center": v(0, -104.25) * mm, "radius": 6 * mm});
            skSolve(sketch);
        }
        {
            var Q0;
            {var subQ0=sQuery(id+"F16.wireOp",EDGE,"E89.MirrorCS");Q0=makeQuery(id+"F16.imprint","IMPRINT",FACE,{"disambiguationData":[TD([[makeQuery(id+"F16.imprint","IMPRINT",EDGE,{"derivedFrom":subQ0}),1.0]])]});}
            var Q1;
            {var subQ3=sQuery(id+"F16.wireOp",EDGE,"E81");Q1=makeQuery(id+"F16.imprint","IMPRINT",FACE,{"disambiguationData":[TD([[makeQuery(id+"F16.imprint","IMPRINT",EDGE,{"derivedFrom":subQ3}),-1.0]])]});}
            var Q2;
            Q2=makeQuery(id+"F16.imprint","IMPRINT",FACE,{"disambiguationData":[TD([[makeQuery(id+"F16.imprint","IMPRINT",EDGE,{"derivedFrom":sQuery(id+"F16.wireOp",EDGE,"E80")}),-1.0]])]});
            var Q3;
            Q3=makeQuery(id+"F2.opExtrude","CAP_FACE",FACE,{"disambiguationData":[OSD([sQuery(id+"F0.wireOp",EDGE,"E12"),sQuery(id+"F0.wireOp",EDGE,"E13"),sQuery(id+"F0.wireOp",EDGE,"E14"),sQuery(id+"F0.wireOp",EDGE,"E15"),sQuery(id+"F0.wireOp",EDGE,"E17.filletArc"),sQuery(id+"F0.wireOp",EDGE,"E18.filletArc"),sQuery(id+"F0.wireOp",EDGE,"E19.filletArc"),sQuery(id+"F0.wireOp",EDGE,"E20.filletArc"),sQuery(id+"F0.wireOp",EDGE,"E25.0"),sQuery(id+"F0.wireOp",EDGE,"E25.1"),sQuery(id+"F0.wireOp",EDGE,"E25.2"),sQuery(id+"F0.wireOp",EDGE,"E25.3"),sQuery(id+"F0.wireOp",EDGE,"E25.4"),sQuery(id+"F0.wireOp",EDGE,"E25.5"),sQuery(id+"F0.wireOp",EDGE,"E25.6"),sQuery(id+"F0.wireOp",EDGE,"E25.7")])],"isStart":false});
            extrude(context, id + "F17", {"entities" : qUnion([Q0, Q1, Q2]), "endBound" : BoundingType.UP_TO_SURFACE, "endBoundEntityFace" : qUnion([Q3]), "depth" : 25 * mm});
        }
    });
